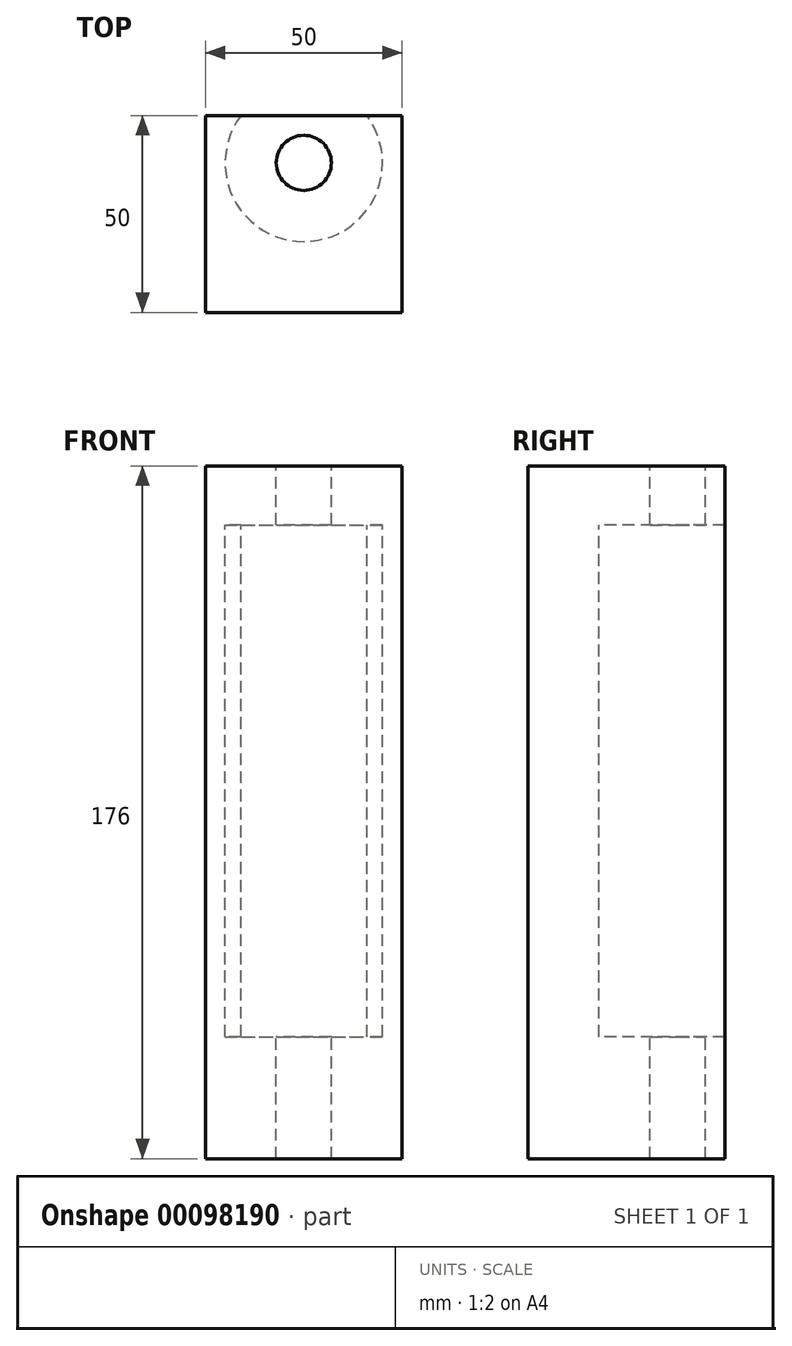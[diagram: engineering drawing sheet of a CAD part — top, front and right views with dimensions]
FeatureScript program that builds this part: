
annotation { "Feature Type Name" : "Feature", "Feature Type Description" : "" }
export const myFeature = defineFeature(function(context is Context, id is Id, definition is map)
    precondition{}
    {
        {
            var Q0;
            Q0=qCreatedBy(makeId("Front.planeOp"),FACE);
            var sketch = newSketch(context, id + "F0", { "sketchPlane" : qUnion([Q0])});
            skLineSegment(sketch, "E0.bottom", {"start": v(0, 176) * mm, "end": v(50, 176) * mm});
            skLineSegment(sketch, "E0.top", {"start": v(0, 0) * mm, "end": v(50, 0) * mm});
            skLineSegment(sketch, "E0.left", {"start": v(0, 176) * mm, "end": v(0, 0) * mm});
            skLineSegment(sketch, "E0.right", {"start": v(50, 176) * mm, "end": v(50, 0) * mm});
            skSolve(sketch);
        }
        {
            var Q0;
            Q0=makeQuery(id+"F0.imprint","IMPRINT",FACE,{"disambiguationData":[TD([[makeQuery(id+"F0.imprint","IMPRINT",EDGE,{"derivedFrom":sQuery(id+"F0.wireOp",EDGE,"E0.bottom")}),-1.0]])]});
            extrude(context, id + "F1", {"entities" : qUnion([Q0]), "oppositeDirection" : true, "depth" : 50 * mm});
        }
        {
            var Q0;
            Q0=makeQuery(id+"F1.opExtrude","SWEPT_FACE",FACE,{"disambiguationData":[OSD([sQuery(id+"F0.wireOp",EDGE,"E0.bottom")])]});
            var sketch = newSketch(context, id + "F2", { "sketchPlane" : qUnion([Q0])});
            skCircle(sketch, "E1", {"center": v(25, 38) * mm, "radius": 7 * mm});
            skCircle(sketch, "E2", {"center": v(25, 38) * mm, "radius": 20 * mm});
            skSolve(sketch);
        }
        {
            var Q0;
            Q0=makeQuery(id+"F2.imprint","IMPRINT",FACE,{"disambiguationData":[TD([[makeQuery(id+"F2.imprint","IMPRINT",EDGE,{"derivedFrom":sQuery(id+"F2.wireOp",EDGE,"E1")}),1.0]])]});
            var Q1;
            Q1=sQuery(id+"F2.wireOp",EDGE,"E1");
            extrude(context, id + "F3", {"entities" : qUnion([Q0]), "operationType" : NewBodyOperationType.REMOVE, "surfaceEntities" : qUnion([Q1]), "endBound" : BoundingType.THROUGH_ALL, "oppositeDirection" : true, "depth" : 25 * mm});
        }
        {
            var Q0;
            Q0=makeQuery(id+"F2.imprint","IMPRINT",FACE,{"disambiguationData":[TD([[makeQuery(id+"F2.imprint","IMPRINT",EDGE,{"derivedFrom":sQuery(id+"F2.wireOp",EDGE,"E1")}),-1.0]])]});
            var Q1;
            Q1=sQuery(id+"F2.wireOp",EDGE,"E2");
            extrude(context, id + "F4", {"entities" : qUnion([Q0]), "operationType" : NewBodyOperationType.REMOVE, "surfaceEntities" : qUnion([Q1]), "oppositeDirection" : true, "depth" : 145 * mm, "hasSecondDirection" : true, "secondDirectionOppositeDirection" : true, "secondDirectionDepth" : 15 * mm});
        }
    });
